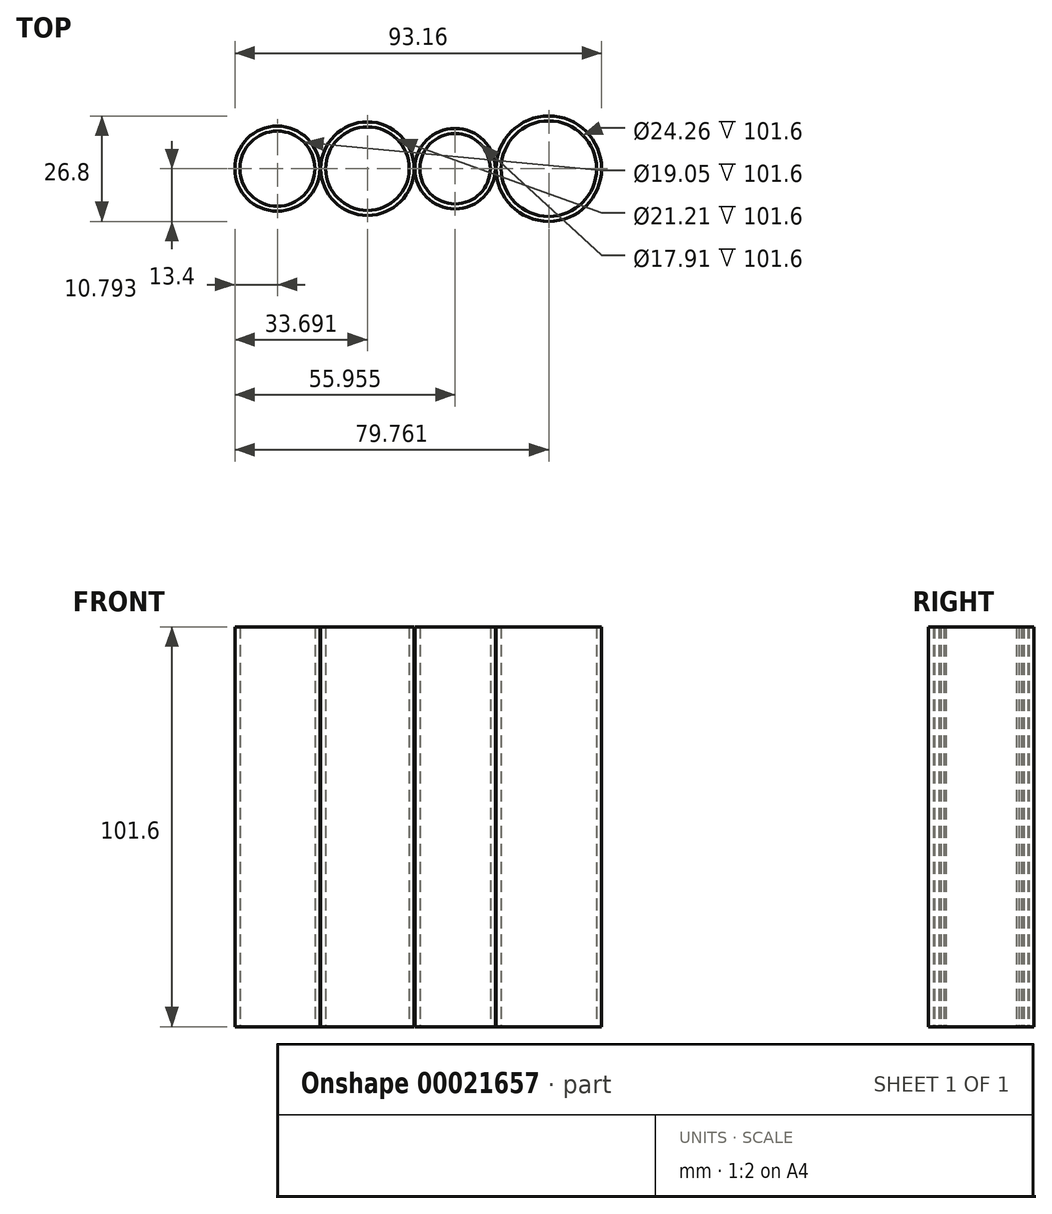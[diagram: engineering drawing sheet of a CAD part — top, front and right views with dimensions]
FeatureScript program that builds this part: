
annotation { "Feature Type Name" : "Feature", "Feature Type Description" : "" }
export const myFeature = defineFeature(function(context is Context, id is Id, definition is map)
    precondition{}
    {
        {
            var Q0;
            Q0=qCreatedBy(makeId("Top.planeOp"),FACE);
            var sketch = newSketch(context, id + "F0", { "sketchPlane" : qUnion([Q0])});
            skCircle(sketch, "E0", {"center": v(-10.78, 0) * mm, "radius": 10.6 * mm});
            skCircle(sketch, "E1", {"center": v(-10.78, 0) * mm, "radius": 11.87 * mm});
            skCircle(sketch, "E2", {"center": v(-33.68, 0) * mm, "radius": 10.8 * mm});
            skCircle(sketch, "E3", {"center": v(-33.68, 0) * mm, "radius": 9.53 * mm});
            skCircle(sketch, "E4", {"center": v(11.48, 0) * mm, "radius": 8.95 * mm});
            skCircle(sketch, "E5", {"center": v(11.48, 0) * mm, "radius": 10.22 * mm});
            skCircle(sketch, "E6", {"center": v(35.3, 0) * mm, "radius": 12.13 * mm});
            skCircle(sketch, "E7", {"center": v(35.3, 0) * mm, "radius": 13.4 * mm});
            skSolve(sketch);
        }
        {
            var Q0;
            Q0=makeQuery(id+"F0.imprint","IMPRINT",FACE,{"disambiguationData":[TD([[makeQuery(id+"F0.imprint","IMPRINT",EDGE,{"derivedFrom":sQuery(id+"F0.wireOp",EDGE,"E0")}),-1.0]])]});
            var Q1;
            Q1=makeQuery(id+"F0.imprint","IMPRINT",FACE,{"disambiguationData":[TD([[makeQuery(id+"F0.imprint","IMPRINT",EDGE,{"derivedFrom":sQuery(id+"F0.wireOp",EDGE,"E2")}),1.0]])]});
            var Q2;
            Q2=makeQuery(id+"F0.imprint","IMPRINT",FACE,{"disambiguationData":[TD([[makeQuery(id+"F0.imprint","IMPRINT",EDGE,{"derivedFrom":sQuery(id+"F0.wireOp",EDGE,"E4")}),-1.0]])]});
            var Q3;
            Q3=makeQuery(id+"F0.imprint","IMPRINT",FACE,{"disambiguationData":[TD([[makeQuery(id+"F0.imprint","IMPRINT",EDGE,{"derivedFrom":sQuery(id+"F0.wireOp",EDGE,"E6")}),-1.0]])]});
            extrude(context, id + "F1", {"entities" : qUnion([Q0, Q1, Q2, Q3]), "depth" : 101.6 * mm});
        }
    });
